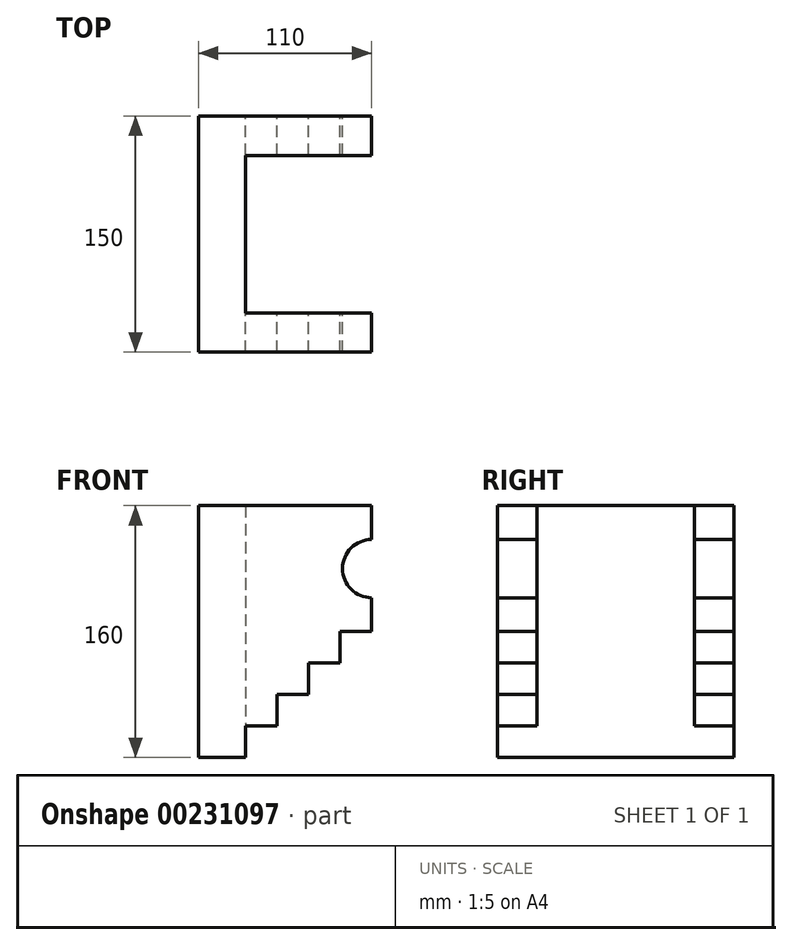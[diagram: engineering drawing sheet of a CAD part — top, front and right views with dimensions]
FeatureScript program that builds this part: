
annotation { "Feature Type Name" : "Feature", "Feature Type Description" : "" }
export const myFeature = defineFeature(function(context is Context, id is Id, definition is map)
    precondition{}
    {
        {
            var Q0;
            Q0=qCreatedBy(makeId("Front.planeOp"),FACE);
            var sketch = newSketch(context, id + "F0", { "sketchPlane" : qUnion([Q0])});
            skLineSegment(sketch, "E0.bottom", {"start": v(0, 0) * mm, "end": v(110, 0) * mm});
            skLineSegment(sketch, "E0.top", {"start": v(0, -160) * mm, "end": v(30, -160) * mm});
            skLineSegment(sketch, "E0.left", {"start": v(0, 0) * mm, "end": v(0, -160) * mm});
            skLineSegment(sketch, "E1", {"start": v(30, -160) * mm, "end": v(30, -140) * mm});
            skLineSegment(sketch, "E2", {"start": v(30, -140) * mm, "end": v(50, -140) * mm});
            skLineSegment(sketch, "E3", {"start": v(50, -140) * mm, "end": v(50, -120) * mm});
            skLineSegment(sketch, "E4", {"start": v(50, -120) * mm, "end": v(70, -120) * mm});
            skLineSegment(sketch, "E5", {"start": v(70, -120) * mm, "end": v(70, -100) * mm});
            skLineSegment(sketch, "E6", {"start": v(70, -100) * mm, "end": v(90, -100) * mm});
            skLineSegment(sketch, "E7", {"start": v(90, -100) * mm, "end": v(90, -80) * mm});
            skLineSegment(sketch, "E8", {"start": v(90, -80) * mm, "end": v(110, -80) * mm});
            skLineSegment(sketch, "E9", {"start": v(110, -80) * mm, "end": v(110, -58.5) * mm});
            skArc(sketch, "E10", {"start": v(110, -21.5) * mm, "mid": v(91.5, -40) * mm, "end": v(110, -58.5) * mm});
            skLineSegment(sketch, "E11.trimOffspring", {"start": v(110, -21.5) * mm, "end": v(110, 0) * mm});
            skSolve(sketch);
        }
        {
            var Q0;
            Q0 = qSketchRegion(id + "F0", true);
            extrude(context, id + "F1", {"entities" : qUnion([Q0]), "depth" : 75 * mm, "hasSecondDirection" : true, "secondDirectionOppositeDirection" : true, "secondDirectionDepth" : 75 * mm});
        }
        {
            var Q0;
            Q0=qCreatedBy(makeId("Right.planeOp"),FACE);
            var sketch = newSketch(context, id + "F2", { "sketchPlane" : qUnion([Q0])});
            skLineSegment(sketch, "E12.bottom", {"start": v(-50, 10) * mm, "end": v(50, 10) * mm});
            skLineSegment(sketch, "E12.top", {"start": v(-50, -190) * mm, "end": v(50, -190) * mm});
            skLineSegment(sketch, "E12.left", {"start": v(-50, 10) * mm, "end": v(-50, -190) * mm});
            skLineSegment(sketch, "E12.right", {"start": v(50, 10) * mm, "end": v(50, -190) * mm});
            skSolve(sketch);
        }
        {
            var Q0;
            Q0 = qSketchRegion(id + "F2", true);
            extrude(context, id + "F3", {"entities" : qUnion([Q0]), "operationType" : NewBodyOperationType.REMOVE, "depth" : 200 * mm, "hasSecondDirection" : true, "secondDirectionOppositeDirection" : false, "secondDirectionDepth" : 30 * mm});
        }
    });
